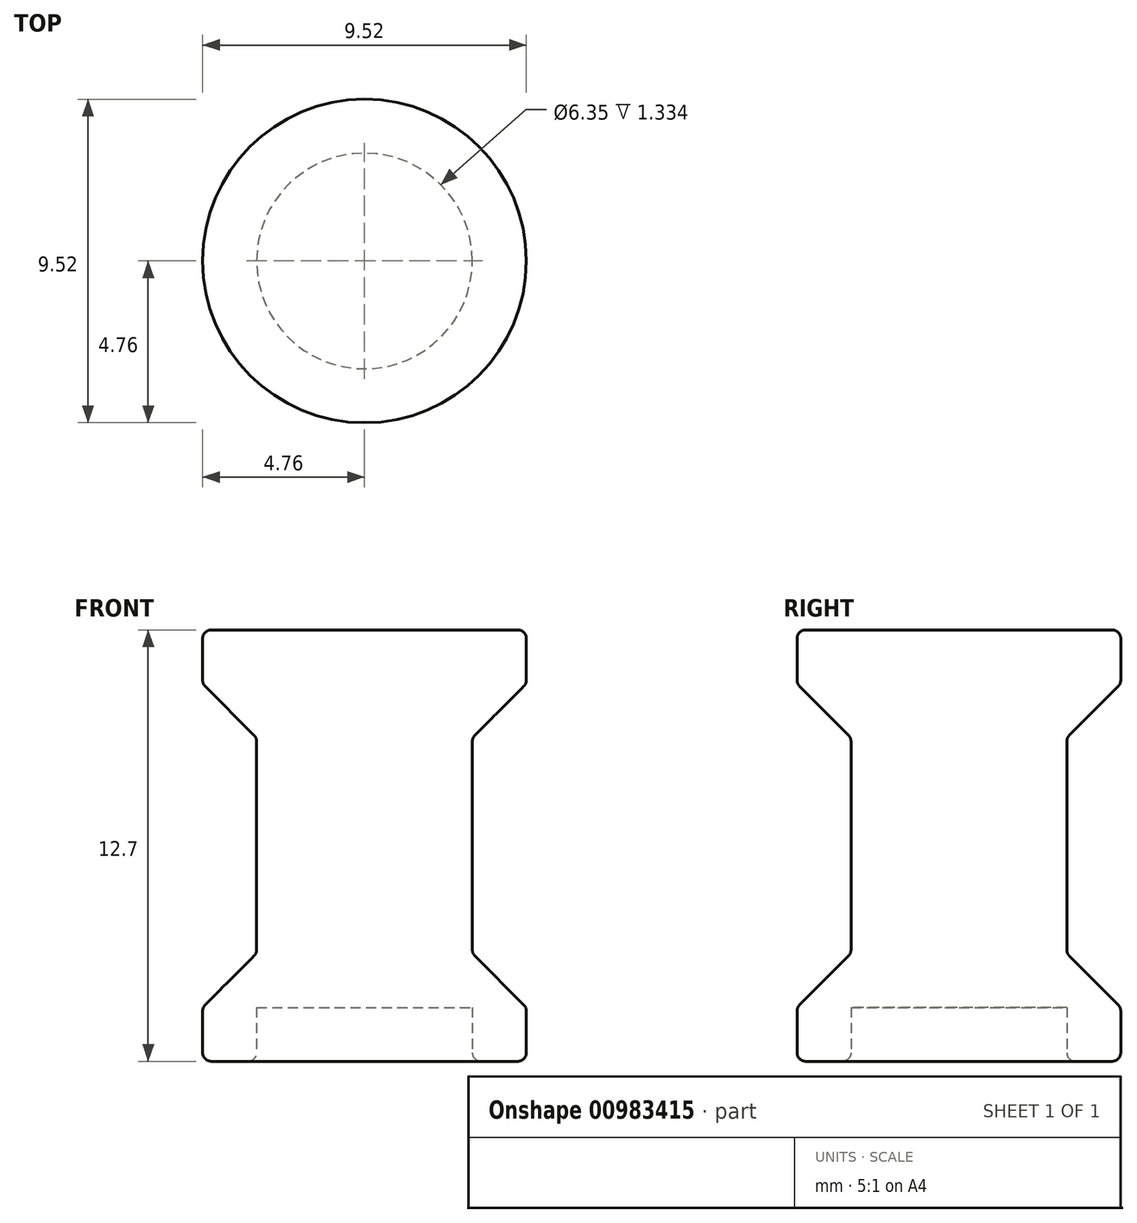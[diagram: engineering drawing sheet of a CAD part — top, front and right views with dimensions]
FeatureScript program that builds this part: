
annotation { "Feature Type Name" : "Feature", "Feature Type Description" : "" }
export const myFeature = defineFeature(function(context is Context, id is Id, definition is map)
    precondition{}
    {
        {
            var Q0;
            Q0=qCreatedBy(makeId("Front.planeOp"),FACE);
            var sketch = newSketch(context, id + "F0", { "sketchPlane" : qUnion([Q0])});
            skLineSegment(sketch, "E0.bottom", {"start": v(0, 0) * mm, "end": v(4.76, 0) * mm, "construction": true});
            skLineSegment(sketch, "E0.top", {"start": v(0, 12.7) * mm, "end": v(4.76, 12.7) * mm, "construction": true});
            skLineSegment(sketch, "E0.left", {"start": v(0, 0) * mm, "end": v(0, 12.7) * mm, "construction": true});
            skLineSegment(sketch, "E0.right", {"start": v(4.76, 0) * mm, "end": v(4.76, 12.7) * mm, "construction": true});
            skLineSegment(sketch, "E1", {"start": v(0, 1.59) * mm, "end": v(3.18, 1.59) * mm, "construction": true});
            skLineSegment(sketch, "E2", {"start": v(3.18, 1.59) * mm, "end": v(3.18, 0) * mm, "construction": true});
            skLineSegment(sketch, "E3", {"start": v(0, 12.7) * mm, "end": v(4.76, 12.7) * mm});
            skLineSegment(sketch, "E4", {"start": v(4.76, 12.7) * mm, "end": v(4.76, 11.11) * mm});
            skLineSegment(sketch, "E5", {"start": v(4.76, 11.11) * mm, "end": v(3.17, 9.53) * mm});
            skLineSegment(sketch, "E6", {"start": v(3.17, 9.52) * mm, "end": v(3.17, 3.17) * mm});
            skLineSegment(sketch, "E7", {"start": v(3.18, 3.17) * mm, "end": v(4.76, 1.59) * mm});
            skLineSegment(sketch, "E8", {"start": v(4.76, 1.59) * mm, "end": v(4.76, 0) * mm});
            skLineSegment(sketch, "E9", {"start": v(3.18, 0) * mm, "end": v(3.18, 1.59) * mm});
            skLineSegment(sketch, "E10", {"start": v(0, 1.59) * mm, "end": v(0, 12.7) * mm});
            skLineSegment(sketch, "E11", {"start": v(0, 1.59) * mm, "end": v(3.18, 1.59) * mm});
            skLineSegment(sketch, "E12", {"start": v(3.18, 0) * mm, "end": v(4.76, 0) * mm});
            skSolve(sketch);
        }
        {
            var Q0;
            Q0=makeQuery(id+"F0.imprint","IMPRINT",FACE,{"disambiguationData":[TD([[makeQuery(id+"F0.imprint","IMPRINT",EDGE,{"derivedFrom":sQuery(id+"F0.wireOp",EDGE,"E3")}),-1.0]])]});
            var Q1;
            Q1=sQuery(id+"F0.wireOp",EDGE,"E0.left");
            revolve(context, id + "F1", {"surfaceOperationType" : NewSurfaceOperationType.NEW, "entities" : qUnion([Q0]), "axis" : qUnion([Q1]), "revolveType" : RevolveType.FULL});
        }
        {
            var Q0;
            Q0=makeQuery(id+"F1.opRevolve","SWEPT_EDGE",EDGE,{"disambiguationData":[OSD([sQuery(id+"F0.wireOp",EDGE,"E9"),sQuery(id+"F0.wireOp",EDGE,"E12")])]});
            var Q1;
            Q1=makeQuery(id+"F1.opRevolve","SWEPT_EDGE",EDGE,{"disambiguationData":[OSD([sQuery(id+"F0.wireOp",EDGE,"E8"),sQuery(id+"F0.wireOp",EDGE,"E12")])]});
            var Q2;
            Q2=makeQuery(id+"F1.opRevolve","SWEPT_EDGE",EDGE,{"disambiguationData":[OSD([sQuery(id+"F0.wireOp",EDGE,"E7"),sQuery(id+"F0.wireOp",EDGE,"E8")])]});
            var Q3;
            Q3=makeQuery(id+"F1.opRevolve","SWEPT_EDGE",EDGE,{"disambiguationData":[OSD([sQuery(id+"F0.wireOp",EDGE,"E6"),sQuery(id+"F0.wireOp",EDGE,"E7")])]});
            var Q4;
            Q4=makeQuery(id+"F1.opRevolve","SWEPT_EDGE",EDGE,{"disambiguationData":[OSD([sQuery(id+"F0.wireOp",EDGE,"E5"),sQuery(id+"F0.wireOp",EDGE,"E6")])]});
            var Q5;
            Q5=makeQuery(id+"F1.opRevolve","SWEPT_EDGE",EDGE,{"disambiguationData":[OSD([sQuery(id+"F0.wireOp",EDGE,"E4"),sQuery(id+"F0.wireOp",EDGE,"E5")])]});
            var Q6;
            Q6=makeQuery(id+"F1.opRevolve","SWEPT_EDGE",EDGE,{"disambiguationData":[OSD([sQuery(id+"F0.wireOp",EDGE,"E3"),sQuery(id+"F0.wireOp",EDGE,"E4")])]});
            fillet(context, id + "F2", {"entities" : qUnion([Q0, Q1, Q2, Q3, Q4, Q5, Q6]), "radius" : 0.25 * mm, "tangentPropagation" : true, "allowEdgeOverflow" : false});
        }
    });
